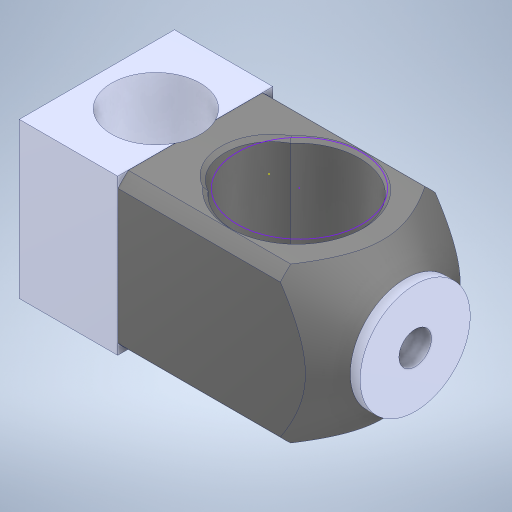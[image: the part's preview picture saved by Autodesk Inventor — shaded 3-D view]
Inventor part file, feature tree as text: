
AUTODESK INVENTOR PART (.ipt)
format: ipt  version: 2023 (Build 270158000, 158)  size: 338,432 bytes
history: mixed  units: in
note: dims shown in document units (in); Inventor stores cm internally (conversion verified against a paired STEP export)
features: sketch x8, extrude x7, other x1, imported_body x1
ambient origin geometry x8: Origin, YZ Plane, XZ Plane, XY Plane, X Axis, Y Axis, Z Axis, Center Point
bodies: Solid1 (imported_parasolid)
feature tree (17):
  other  "6669-001-1-solid1"
  extrude  "Extrusion1"  Depth=0.3937in
  sketch  "Sketch2"  dims[d8=0.3937in d9=0.0in d10=0.0in d11=0.0in]
  extrude  "Extrusion4"  TaperAngle=0.0deg  [1 undecoded]
  sketch  "Sketch5"  dims[d16=0.2362in d17=0.1969in]
  extrude  "Extrusion5"  Depth=0.3937in TaperAngle=0.0deg
  extrude  "Extrusion6"  Depth=0.1969in
  extrude  "Extrusion7"  Depth=0.3543in
  extrude  "Extrusion8"  Depth=0.0197in
  extrude  "Extrusion9"  Depth=0.0197in
  sketch  "Sketch1"  dims[d0=0.3937in d1=0.0in d7=0.1299in]
  sketch  "Sketch4"  dims[d12=0.0394in d13=0.0in d14=0.3937in d15=0.0in]
  sketch  "Sketch6"  dims[d18=0.1969in d19=0.0in d20=0.3543in]
  sketch  "Sketch7"  dims[d21=0.0in d22=0.0in d2=0.0197in]
  sketch  "Sketch8"  dims[d3=0.0344in d4=0.0197in]
  sketch  "Sketch9"  dims[d5=0.0344in]
  imported_body  NMx_Import_Brep_tag  [imported B-rep: ~14 faces, bbox_mm=[22.836, 10.765997, 12.379599]]
note: 1 required parameter value undecoded (feature->parameter linkage not recoverable at this tier; creation-order binding heuristic only, values carry confidence <= 0.55)
